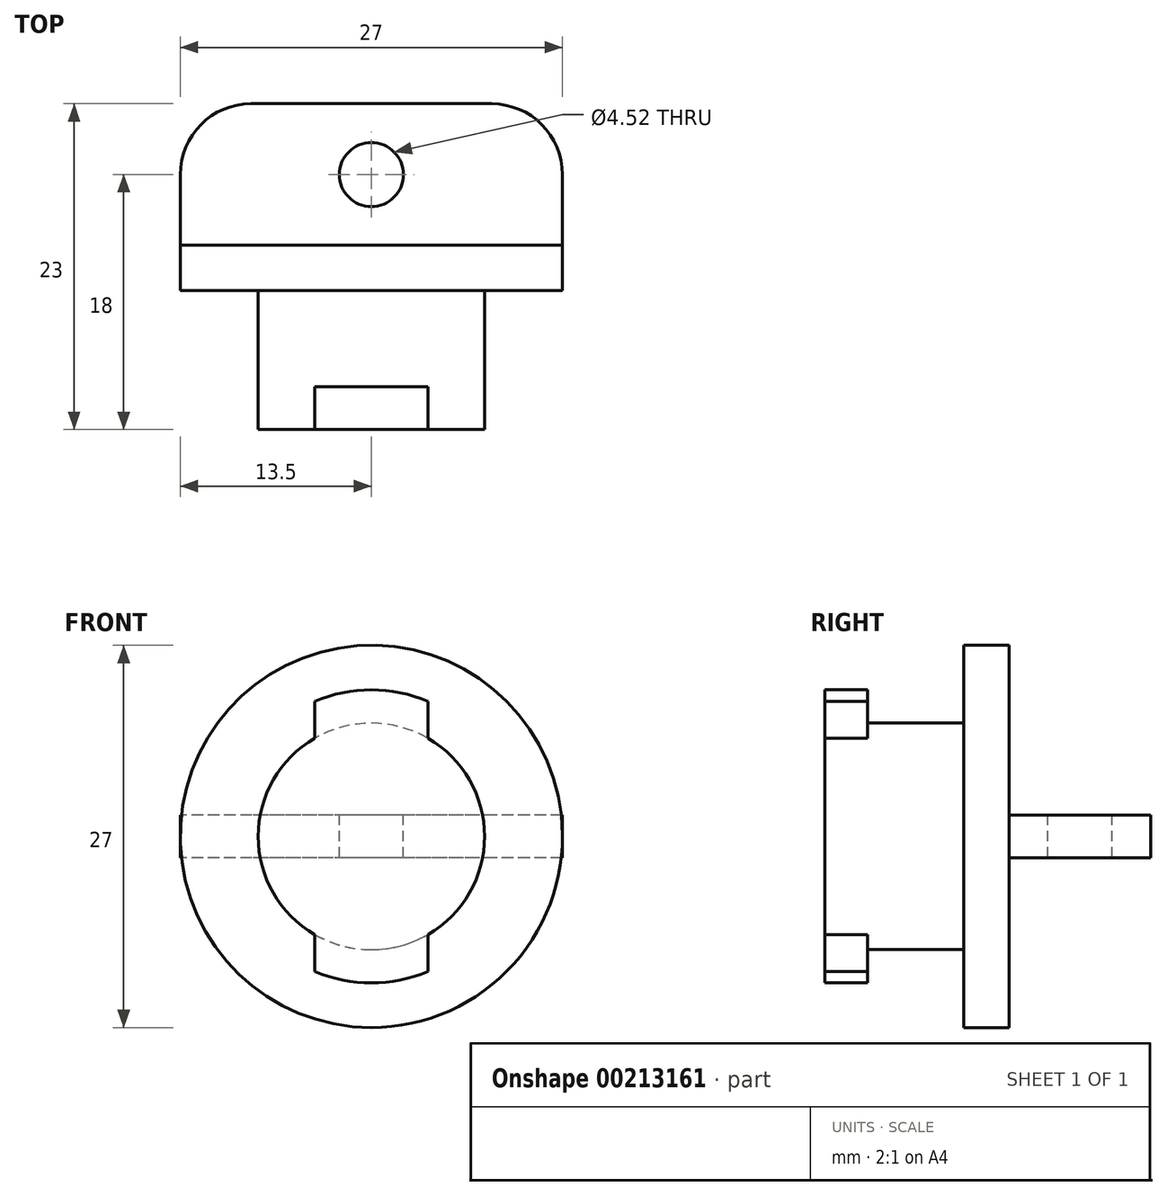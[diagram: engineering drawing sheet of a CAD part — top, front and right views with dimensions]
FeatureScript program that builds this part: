
annotation { "Feature Type Name" : "Feature", "Feature Type Description" : "" }
export const myFeature = defineFeature(function(context is Context, id is Id, definition is map)
    precondition{}
    {
        {
            var Q0;
            Q0=qCreatedBy(makeId("Front.planeOp"),FACE);
            var sketch = newSketch(context, id + "F0", { "sketchPlane" : qUnion([Q0])});
            skCircle(sketch, "E0", {"center": v(0, 0) * mm, "radius": 13.5 * mm});
            skCircle(sketch, "E1", {"center": v(0, 0) * mm, "radius": 8 * mm});
            skSolve(sketch);
        }
        {
            var Q0;
            Q0=makeQuery(id+"F0.imprint","IMPRINT",FACE,{"disambiguationData":[TD([[makeQuery(id+"F0.imprint","IMPRINT",EDGE,{"derivedFrom":sQuery(id+"F0.wireOp",EDGE,"E1")}),1.0]])]});
            extrude(context, id + "F1", {"entities" : qUnion([Q0]), "depth" : 13 * mm});
        }
        {
            var Q0;
            Q0 = qSketchRegion(id + "F0", true);
            extrude(context, id + "F2", {"entities" : qUnion([Q0]), "operationType" : NewBodyOperationType.ADD, "depth" : 3.2 * mm});
        }
        {
            var Q0;
            Q0=makeQuery(id+"F2.opExtrude","CAP_FACE",FACE,{"disambiguationData":[OSD([sQuery(id+"F0.wireOp",EDGE,"E0"),sQuery(id+"F0.wireOp",EDGE,"E1")])],"isStart":false});
            cPlane(context, id + "F3", {"entities" : qUnion([Q0]), "cplaneType" : CPlaneType.OFFSET, "offset" : 6.8 * mm, "width" : 150 * mm, "height" : 150 * mm});
        }
        {
            var Q0;
            Q0=qCreatedBy(id+"F3.planeOp",FACE);
            var sketch = newSketch(context, id + "F4", { "sketchPlane" : qUnion([Q0])});
            skLineSegment(sketch, "E2.bottom", {"start": v(4, -10.35) * mm, "end": v(-4, -10.35) * mm});
            skLineSegment(sketch, "E2.top", {"start": v(4, 10.35) * mm, "end": v(-4, 10.35) * mm});
            skLineSegment(sketch, "E2.left", {"start": v(4, -10.35) * mm, "end": v(4, 10.35) * mm});
            skLineSegment(sketch, "E2.right", {"start": v(-4, -10.35) * mm, "end": v(-4, 10.35) * mm});
            skPoint(sketch, "E2.middle", {"position": v(0, 0) * mm});
            skCircle(sketch, "E3", {"center": v(0, 0) * mm, "radius": 10.35 * mm});
            skSolve(sketch);
        }
        {
            var Q0;
            {var subQ0=sQuery(id+"F4.wireOp",EDGE,"E3");var subQ5=sQuery(id+"F4.wireOp",EDGE,"E2.left");var subQ6=makeQuery(id+"F4.imprint","INTERSECT",VERTEX,{"disambiguationData":[OD(0.0)],"derivedFrom":[subQ5,subQ0]});Q0=makeQuery(id+"F4.imprint","IMPRINT",FACE,{"disambiguationData":[TD([[makeQuery(id+"F4.imprint","IMPRINT",EDGE,{"disambiguationData":[TD([[subQ6,-1.0]])],"derivedFrom":subQ5}),1.0]])]});}
            extrude(context, id + "F5", {"entities" : qUnion([Q0]), "operationType" : NewBodyOperationType.ADD, "depth" : 3 * mm});
        }
        {
            var Q0;
            Q0=qCreatedBy(makeId("Front.planeOp"),FACE);
            var sketch = newSketch(context, id + "F6", { "sketchPlane" : qUnion([Q0])});
            skLineSegment(sketch, "E4.bottom", {"start": v(13.5, -1.5) * mm, "end": v(-13.5, -1.5) * mm});
            skLineSegment(sketch, "E4.top", {"start": v(13.5, 1.5) * mm, "end": v(-13.5, 1.5) * mm});
            skLineSegment(sketch, "E4.left", {"start": v(13.5, -1.5) * mm, "end": v(13.5, 1.5) * mm});
            skLineSegment(sketch, "E4.right", {"start": v(-13.5, -1.5) * mm, "end": v(-13.5, 1.5) * mm});
            skPoint(sketch, "E4.middle", {"position": v(0, 0) * mm});
            skSolve(sketch);
        }
        {
            var Q0;
            Q0=makeQuery(id+"F6.imprint","IMPRINT",FACE,{"disambiguationData":[TD([[makeQuery(id+"F6.imprint","IMPRINT",EDGE,{"derivedFrom":sQuery(id+"F6.wireOp",EDGE,"E4.bottom")}),-1.0]])]});
            extrude(context, id + "F7", {"entities" : qUnion([Q0]), "operationType" : NewBodyOperationType.ADD, "oppositeDirection" : true, "depth" : 10 * mm});
        }
        {
            var Q0;
            Q0=makeQuery(id+"F7.opExtrude","CAP_EDGE",EDGE,{"disambiguationData":[OSD([sQuery(id+"F6.wireOp",EDGE,"E4.right")])],"isStart":false});
            fillet(context, id + "F8", {"entities" : qUnion([Q0]), "radius" : 5 * mm, "tangentPropagation" : true, "allowEdgeOverflow" : false});
        }
        {
            var Q0;
            Q0=makeQuery(id+"F7.opExtrude","CAP_EDGE",EDGE,{"disambiguationData":[OSD([sQuery(id+"F6.wireOp",EDGE,"E4.left")])],"isStart":false});
            fillet(context, id + "F9", {"entities" : qUnion([Q0]), "radius" : 5 * mm, "tangentPropagation" : true, "allowEdgeOverflow" : false});
        }
        {
            var Q0;
            Q0=makeQuery(id+"F7.opExtrude","SWEPT_FACE",FACE,{"disambiguationData":[OSD([sQuery(id+"F6.wireOp",EDGE,"E4.top")])]});
            var sketch = newSketch(context, id + "F10", { "sketchPlane" : qUnion([Q0])});
            skSolve(sketch);
        }
        {
            var Q0;
            {var subQ1=sQuery(id+"F6.wireOp",EDGE,"E4.top");Q0=makeQuery(id+"F10.imprint","IMPRINT",FACE,{"disambiguationData":[TD([[makeQuery(id+"F10.imprint","IMPRINT",EDGE,{"derivedFrom":makeQuery(id+"F7.opExtrude","CAP_EDGE",EDGE,{"disambiguationData":[OSD([subQ1])],"isStart":false})}),1.0]])]});}
            var sketch = newSketch(context, id + "F11", { "sketchPlane" : qUnion([Q0])});
            skCircle(sketch, "E5", {"center": v(0, 5) * mm, "radius": 2.26 * mm});
            skSolve(sketch);
        }
        {
            var Q0;
            Q0=makeQuery(id+"F11.imprint","IMPRINT",FACE,{"disambiguationData":[TD([[makeQuery(id+"F11.imprint","IMPRINT",EDGE,{"derivedFrom":sQuery(id+"F11.wireOp",EDGE,"E5")}),1.0]])]});
            extrude(context, id + "F12", {"entities" : qUnion([Q0]), "operationType" : NewBodyOperationType.REMOVE, "endBound" : BoundingType.UP_TO_NEXT, "oppositeDirection" : true, "depth" : 25 * mm});
        }
    });
